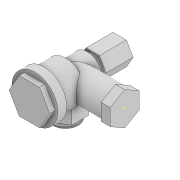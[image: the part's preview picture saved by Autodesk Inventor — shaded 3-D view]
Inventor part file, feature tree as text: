
AUTODESK INVENTOR PART (.ipt)
format: ipt  version: 2022 (Build 260153000, 153)  size: 243,712 bytes
history: native  units: mm
features: extrude x12, sketch x12, thread x2, other x2, projected_geometry x2, plane x1, loft x1
ambient origin geometry x8: Origin, YZ Plane, XZ Plane, XY Plane, X Axis, Y Axis, Z Axis, Center Point
bodies: Solid1 (feature_tree)
feature tree (32):
  extrude  "Extrusion1"  Depth=3.0mm TaperAngle=0.0deg
  extrude  "Extrusion2"  Depth=8.0mm TaperAngle=0.0deg
  extrude  "Extrusion3"  Depth=3.0mm TaperAngle=0.0deg
  plane  "Work Plane1"
  extrude  "Extrusion4"  TaperAngle=0.0deg  [1 undecoded]
  loft  "Loft1"
  extrude  "Extrusion5"  Depth=5.0mm TaperAngle=0.0deg
  extrude  "Extrusion6"  Depth=3.0mm TaperAngle=0.0deg
  extrude  "Extrusion7"  Depth=3.0mm TaperAngle=0.0deg
  extrude  "Extrusion8"  Depth=3.0mm TaperAngle=0.0deg
  extrude  "Extrusion9"  [1 undecoded]
  extrude  "Extrusion10"  [1 undecoded]
  extrude  "Extrusion11"  [1 undecoded]
  thread  "Thread1"  [1 undecoded]
  extrude  "Extrusion12"  [1 undecoded]
  thread  "Thread2"  [1 undecoded]
  sketch  "Sketch1"  dims[d0=14.0mm d1=3.0mm d2=0.0mm]
  sketch  "Sketch2"  dims[d3=8.0mm d4=0.0mm d5=12.0mm d6=0.0mm]
  sketch  "Sketch3"  dims[d7=3.0mm d8=9.0mm d9=0.0mm]
  sketch  "Sketch4"  dims[d10=0.0mm d11=90.0deg d12=0.0mm d13=90.0deg]
  other  "Edges1"
  other  "Edges2"
  sketch  "Sketch5"  dims[d14=9.0mm d15=0.0mm d16=10.0mm d17=0.0mm]
  projected_geometry  "Projected Loop1"
  projected_geometry  "Projected Loop2"
  sketch  "Sketch6"  dims[d18=16.75mm d19=0.0mm d20=5.0mm d21=0.0mm]
  sketch  "Sketch7"  dims[d22=5.0mm d23=0.0mm d24=3.0mm d25=0.0mm]
  sketch  "Sketch8"  dims[d26=3.0mm d27=0.0mm d28=3.0mm d29=0.0mm]
  sketch  "Sketch9"  dims[d30=15.0mm d31=0.0mm d32=3.0mm d33=0.0mm]
  sketch  "Sketch10"
  sketch  "Sketch11"
  sketch  "Sketch12"
note: 7 required parameter values undecoded (feature->parameter linkage not recoverable at this tier; creation-order binding heuristic only, values carry confidence <= 0.55)
